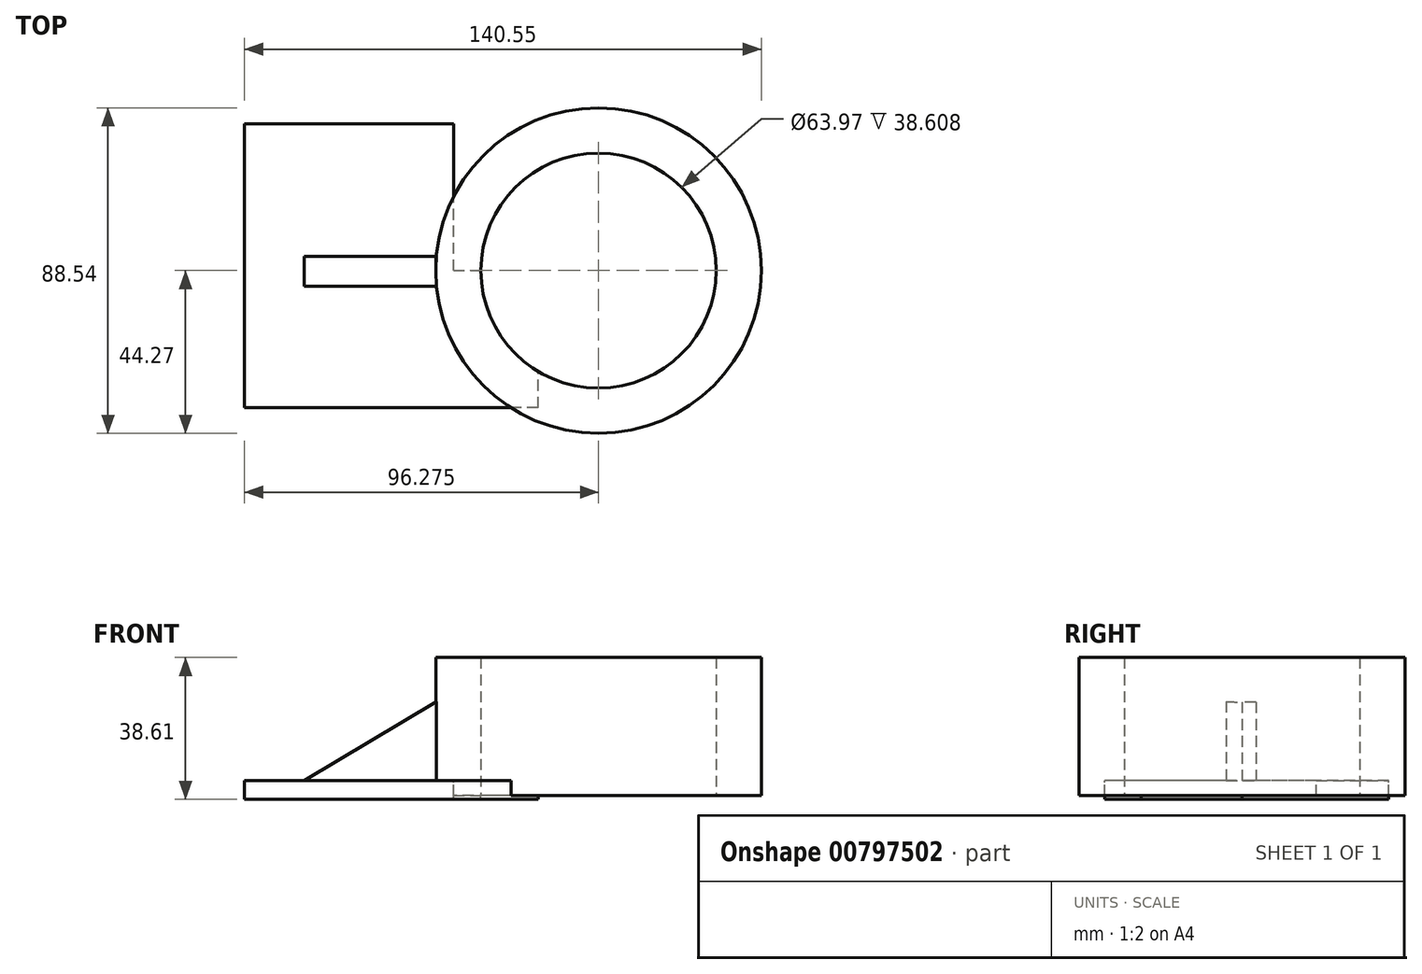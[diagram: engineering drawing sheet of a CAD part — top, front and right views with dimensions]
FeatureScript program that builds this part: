
annotation { "Feature Type Name" : "Feature", "Feature Type Description" : "" }
export const myFeature = defineFeature(function(context is Context, id is Id, definition is map)
    precondition{}
    {
        {
            var Q0;
            Q0=qCreatedBy(makeId("Top.planeOp"),FACE);
            var sketch = newSketch(context, id + "F0", { "sketchPlane" : qUnion([Q0])});
            skLineSegment(sketch, "E0.bottom", {"start": v(0, 0) * mm, "end": v(-56.86, 0) * mm});
            skLineSegment(sketch, "E0.top", {"start": v(0, 39.93) * mm, "end": v(-56.86, 39.93) * mm});
            skLineSegment(sketch, "E0.left", {"start": v(0, 0) * mm, "end": v(0, 39.93) * mm});
            skLineSegment(sketch, "E0.right", {"start": v(-56.86, 0) * mm, "end": v(-56.86, 39.93) * mm});
            skLineSegment(sketch, "E1.top", {"start": v(0, -37.33) * mm, "end": v(-56.86, -37.33) * mm});
            skLineSegment(sketch, "E1.left", {"start": v(0, 0) * mm, "end": v(0, -37.33) * mm});
            skLineSegment(sketch, "E1.right", {"start": v(-56.86, 0) * mm, "end": v(-56.86, -37.33) * mm});
            skLineSegment(sketch, "E2.bottom", {"start": v(0, -37.33) * mm, "end": v(23, -37.33) * mm});
            skLineSegment(sketch, "E2.top", {"start": v(0, 0) * mm, "end": v(23, 0) * mm});
            skLineSegment(sketch, "E2.left", {"start": v(0, -37.33) * mm, "end": v(0, 0) * mm});
            skLineSegment(sketch, "E2.right", {"start": v(23, -37.33) * mm, "end": v(23, 0) * mm});
            skLineSegment(sketch, "E3.bottom", {"start": v(23, 0) * mm, "end": v(0, 0) * mm});
            skLineSegment(sketch, "E3.top", {"start": v(23, 39.93) * mm, "end": v(0, 39.93) * mm});
            skLineSegment(sketch, "E3.left", {"start": v(23, 0) * mm, "end": v(23, 39.93) * mm});
            skSolve(sketch);
        }
        {
            var Q0;
            Q0=makeQuery(id+"F0.imprint","IMPRINT",FACE,{"disambiguationData":[TD([[makeQuery(id+"F0.imprint","IMPRINT",EDGE,{"derivedFrom":sQuery(id+"F0.wireOp",EDGE,"E0.bottom")}),1.0]])]});
            var Q1;
            Q1=makeQuery(id+"F0.imprint","IMPRINT",FACE,{"disambiguationData":[TD([[makeQuery(id+"F0.imprint","IMPRINT",EDGE,{"derivedFrom":sQuery(id+"F0.wireOp",EDGE,"E0.top")}),1.0]])]});
            var Q2;
            Q2=makeQuery(id+"F0.imprint","IMPRINT",FACE,{"disambiguationData":[TD([[makeQuery(id+"F0.imprint","IMPRINT",EDGE,{"derivedFrom":sQuery(id+"F0.wireOp",EDGE,"E3.bottom")}),-1.0]])]});
            var Q3;
            Q3=makeQuery(id+"F0.imprint","IMPRINT",FACE,{"disambiguationData":[TD([[makeQuery(id+"F0.imprint","IMPRINT",EDGE,{"derivedFrom":sQuery(id+"F0.wireOp",EDGE,"E2.bottom")}),1.0]])]});
            extrude(context, id + "F1", {"entities" : qUnion([Q0, Q1, Q2, Q3]), "oppositeDirection" : true, "depth" : 5.08 * mm, "offsetDistance" : 25.4 * mm});
        }
        {
            var Q0;
            Q0=makeQuery(id+"F1.opExtrude","CAP_FACE",FACE,{"disambiguationData":[OSD([sQuery(id+"F0.wireOp",EDGE,"E0.top"),sQuery(id+"F0.wireOp",EDGE,"E0.right"),sQuery(id+"F0.wireOp",EDGE,"E1.top"),sQuery(id+"F0.wireOp",EDGE,"E1.right"),sQuery(id+"F0.wireOp",EDGE,"E2.bottom"),sQuery(id+"F0.wireOp",EDGE,"E2.right"),sQuery(id+"F0.wireOp",EDGE,"E3.top"),sQuery(id+"F0.wireOp",EDGE,"E3.left")])],"isStart":true});
            var sketch = newSketch(context, id + "F2", { "sketchPlane" : qUnion([Q0])});
            skLineSegment(sketch, "E4", {"start": v(0, 0) * mm, "end": v(39.42, 0) * mm});
            skCircle(sketch, "E5", {"center": v(39.42, 0) * mm, "radius": 44.27 * mm});
            skCircle(sketch, "E6", {"center": v(39.42, 0) * mm, "radius": 31.98 * mm});
            skSolve(sketch);
        }
        {
            var Q0;
            Q0 = qSketchRegion(id + "F2", true);
            var Q1;
            {var subQ0=sQuery(id+"F2.wireOp",EDGE,"E6");var subQ1=makeQuery(id+"F2.imprint","INTERSECT",VERTEX,{"derivedFrom":[sQuery(id+"F2.wireOp",EDGE,"E4"),subQ0]});Q1=makeQuery(id+"F2.imprint","IMPRINT",FACE,{"disambiguationData":[TD([[makeQuery(id+"F2.imprint","IMPRINT",EDGE,{"disambiguationData":[TD([[subQ1,1.0]])],"derivedFrom":subQ0}),-1.0]])]});}
            extrude(context, id + "F3", {"entities" : qUnion([Q0, Q1]), "operationType" : NewBodyOperationType.ADD, "depth" : 33.53 * mm, "offsetDistance" : 25.4 * mm});
        }
        {
            var Q0;
            Q0=makeQuery(id+"F3.opExtrude","CAP_FACE",FACE,{"disambiguationData":[OSD([sQuery(id+"F2.wireOp",EDGE,"E5"),sQuery(id+"F2.wireOp",EDGE,"E6")])],"isStart":true});
            extrude(context, id + "F4", {"entities" : qUnion([Q0]), "operationType" : NewBodyOperationType.ADD, "depth" : 4.06 * mm, "offsetDistance" : 25.4 * mm});
        }
        {
            var Q0;
            {var subQ0=sQuery(id+"F0.wireOp",EDGE,"E3.left");var subQ1=sQuery(id+"F0.wireOp",EDGE,"E2.right");var subQ2=sQuery(id+"F2.wireOp",EDGE,"E6");Q0=makeQuery(id+"F3.boolean.opBoolean","SPLIT",FACE,{"disambiguationData":[TD([makeQuery(id+"F3.opExtrude","SWEPT_FACE",FACE,{"disambiguationData":[OSD([subQ2])]})])],"derivedFrom":makeQuery(id+"F1.opExtrude","CAP_FACE",FACE,{"disambiguationData":[OSD([sQuery(id+"F0.wireOp",EDGE,"E0.top"),sQuery(id+"F0.wireOp",EDGE,"E0.right"),sQuery(id+"F0.wireOp",EDGE,"E1.top"),sQuery(id+"F0.wireOp",EDGE,"E1.right"),sQuery(id+"F0.wireOp",EDGE,"E2.bottom"),subQ1,sQuery(id+"F0.wireOp",EDGE,"E3.top"),subQ0])],"isStart":true})});}
            extrude(context, id + "F5", {"entities" : qUnion([Q0]), "operationType" : NewBodyOperationType.REMOVE, "oppositeDirection" : true, "depth" : 123.7 * mm, "offsetDistance" : 25.4 * mm});
        }
        {
            var Q0;
            Q0=qCreatedBy(makeId("Front.planeOp"),FACE);
            var sketch = newSketch(context, id + "F6", { "sketchPlane" : qUnion([Q0])});
            skLineSegment(sketch, "E7", {"start": v(0, 0) * mm, "end": v(0, 24.3) * mm});
            skLineSegment(sketch, "E8", {"start": v(0, 24.3) * mm, "end": v(-40.67, 0) * mm});
            skLineSegment(sketch, "E9", {"start": v(-40.67, 0) * mm, "end": v(0, 0) * mm});
            skSolve(sketch);
        }
        {
            var Q0;
            Q0=makeQuery(id+"F6.imprint","IMPRINT",FACE,{"disambiguationData":[TD([[makeQuery(id+"F6.imprint","IMPRINT",EDGE,{"derivedFrom":sQuery(id+"F6.wireOp",EDGE,"E7")}),1.0]])]});
            extrude(context, id + "F7", {"entities" : qUnion([Q0]), "operationType" : NewBodyOperationType.ADD, "depth" : 4.32 * mm, "offsetDistance" : 25.4 * mm});
        }
        {
            var Q0;
            Q0=makeQuery(id+"F7.opExtrude","CAP_FACE",FACE,{"disambiguationData":[OSD([sQuery(id+"F6.wireOp",EDGE,"E7"),sQuery(id+"F6.wireOp",EDGE,"E8"),sQuery(id+"F6.wireOp",EDGE,"E9")])],"isStart":true});
            extrude(context, id + "F8", {"entities" : qUnion([Q0]), "operationType" : NewBodyOperationType.ADD, "depth" : 3.8 * mm, "offsetDistance" : 25.4 * mm});
        }
    });
